# Revit family: IRB 200 E1 ErP AC_7880037
name_source: partatom
category: Mechanical Equipment
revit_build: Autodesk Revit MEP 2014 (Build: 20130308_1515(x64)
units: mm (PartAtom-declared; Revit-internal decimal feet)

## types (1)
- IRB 200 E1 ErP AC
    Capacitor = 6
    Current = 1 A
    Depth = 308 mm  [stored 1.0105 ft]
    Description = Insulated duct fans with circular connections
    Diameter = 200 mm  [stored 0.656168 ft]
    Frequency = 50 Hz
    Height = 507 mm  [stored 1.66339 ft]
    Main Material = Steel, Galvanized
    Max. temperature of transported air = 60 °C
    Max. temperature of transported air when speed controlled = 60 °C
    Phase = 1
    Power = 209 W
    Sound pressure level at 3 m = 49 dB(A)
    Speed = 2790 rpm
    Voltage = 230 V
    Voltage range = 220-240
    Weight = 20.20 kg
    Width = 702 mm  [stored 2.30315 ft]
    Wiring diagram = 4040001

note: [stored X ft] marks values corroborated as IEEE doubles in the binary element streams (Revit-internal decimal feet)

## geometry (parser evidence)
native form markers: Sweep x2
no freeform markers — native parametric forms only
